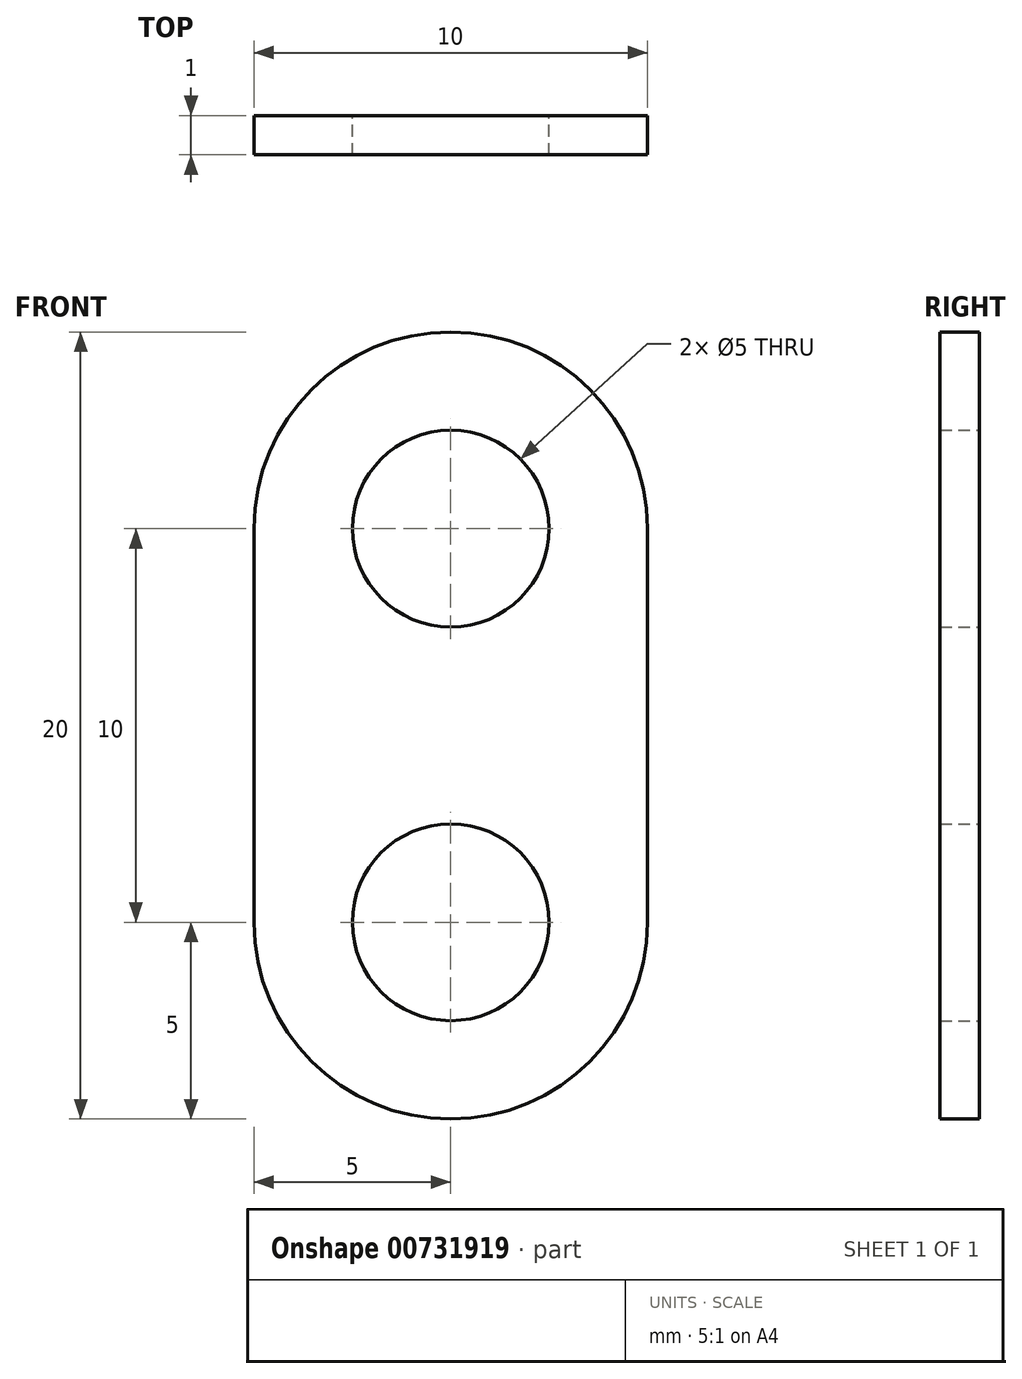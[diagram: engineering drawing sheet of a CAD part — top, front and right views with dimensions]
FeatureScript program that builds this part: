
annotation { "Feature Type Name" : "Feature", "Feature Type Description" : "" }
export const myFeature = defineFeature(function(context is Context, id is Id, definition is map)
    precondition{}
    {
        {
            var Q0;
            Q0=qCreatedBy(makeId("Front.planeOp"),FACE);
            var sketch = newSketch(context, id + "F0", { "sketchPlane" : qUnion([Q0])});
            skArc(sketch, "E0", {"start": v(5, 0) * mm, "mid": v(0, 5) * mm, "end": v(-5, 0) * mm});
            skArc(sketch, "E1", {"start": v(-5, -10) * mm, "mid": v(0, -15) * mm, "end": v(5, -10) * mm});
            skCircle(sketch, "E2", {"center": v(0, 0) * mm, "radius": 2.5 * mm});
            skCircle(sketch, "E3", {"center": v(0, -10) * mm, "radius": 2.5 * mm});
            skLineSegment(sketch, "E4", {"start": v(-5, -10) * mm, "end": v(-5, 0) * mm});
            skLineSegment(sketch, "E5", {"start": v(5, -10) * mm, "end": v(5, 0) * mm});
            skSolve(sketch);
        }
        {
            var Q0;
            Q0=qSketchRegion(id+"F0",true);
            extrude(context, id + "F1", {"entities" : qUnion([Q0]), "depth" : 1 * mm, "offsetDistance" : 25.4 * mm});
        }
    });
